# Revit family: A
name_source: partatom
category: Specialty Equipment
units: mm (PartAtom-declared; Revit-internal decimal feet)

## family parameters
Cut with Voids When Loaded = No
Host = Face
Maintain Annotation Orientation = No
OmniClass Number = 23.31.25.00
Part Type = Normal
Room Calculation Point = No
Round Connector Dimension = Use Diameter
Shared = No

## types (6) — shared parameters
ADA Compliant = No
Assembly Code = C1030200
Date Modified = 08/15/2024
Default Elevation = 42"
Description = Soap Dish
Height = 1 13/16"
Length = 4 13/16"
Manufacturer = Kohler Co.
Master Format 2014 = 10 28 00
Master Format 2014 Name = Toilet, Bath, and Laundry Accessories
Material = Premium Metal Construction
Product Name = Accent
URL = https://www.kohler.co.in
WaterSense Certified = No
Width = 4 3/16"

## per-type parameters (varying)
| type | Finish | Model | Type |
| BN-Vibrant Brushed Nickel | Kohler-Metal-BN-Vibrant_Brushed_Nickel | K-25429IN-BN | 1 |
| BL-Matte Black | Kohler-Metal-BL-Matte_Black | K-25429IN-BL | 2 |
| RGD-Polished Rose Gold | Kohler-Metal-RGD-Polished_Rose_Gold | K-25429IN-RGD | 3 |
| BV-Brushed Bronze | Kohler-Metal-BV-Brushed_Bronze | K-25429IN-BV | 4 |
| AF-Vibrant French Gold | Kohler-Metal-AF-Vibrant_French_Gold | K-25429IN-AF | 5 |
| BRD-Brushed Rose Gold | KOHLER-Metal-BRD-Brushed_Rose_Gold | K-25429IN-BRD | 6 |

## geometry (parser evidence)
native form markers: Sweep x4
no freeform markers — native parametric forms only
